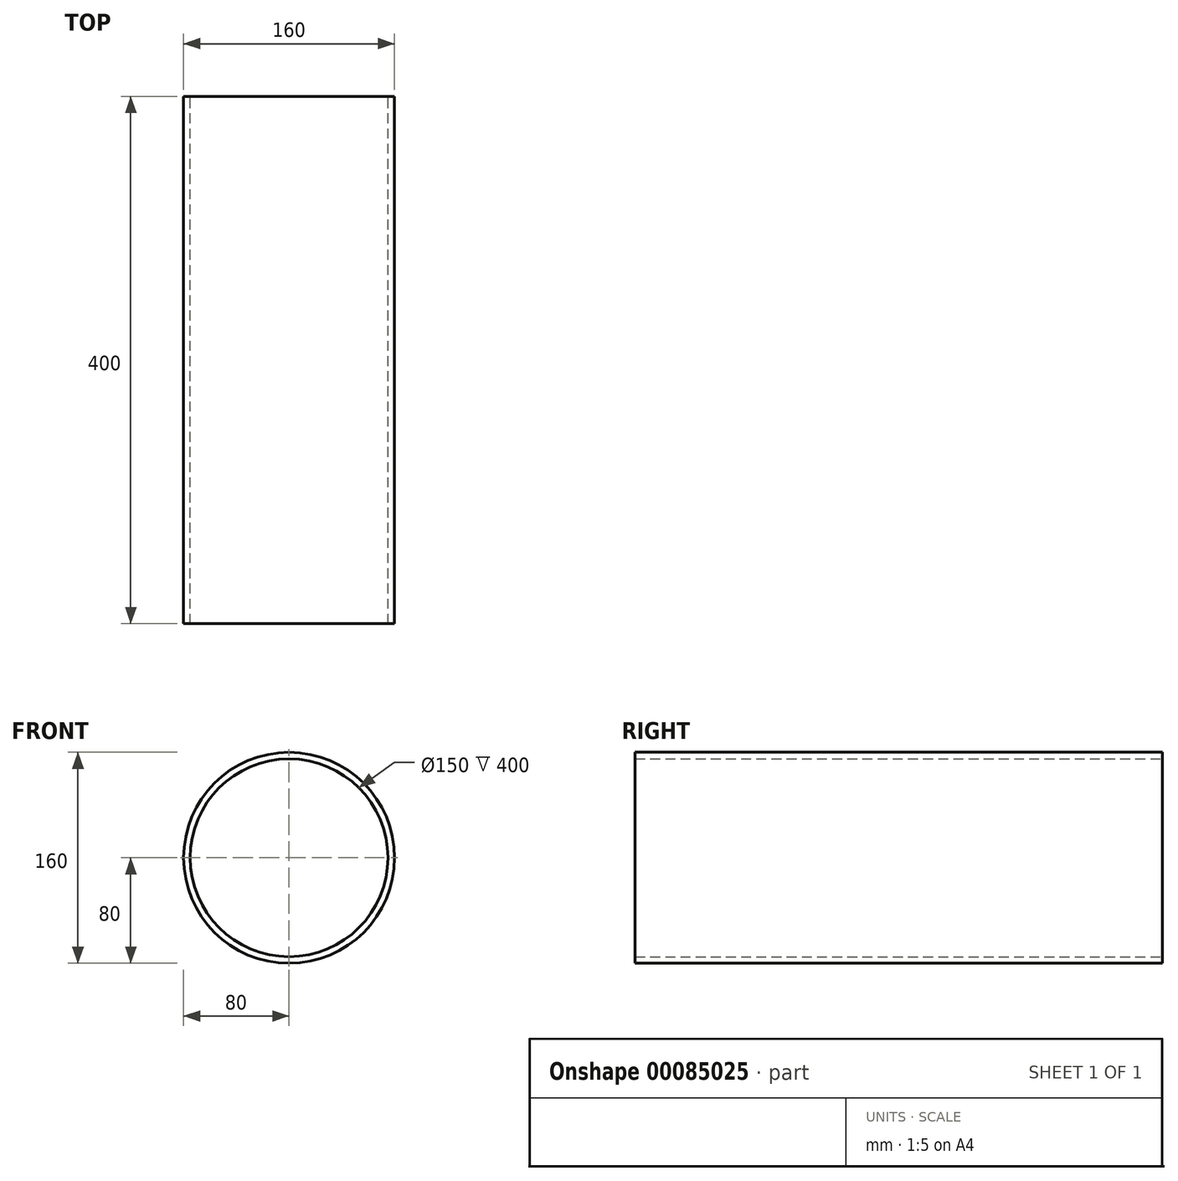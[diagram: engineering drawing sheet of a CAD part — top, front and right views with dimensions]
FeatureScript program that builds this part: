
annotation { "Feature Type Name" : "Feature", "Feature Type Description" : "" }
export const myFeature = defineFeature(function(context is Context, id is Id, definition is map)
    precondition{}
    {
        {
            var Q0;
            Q0=qCreatedBy(makeId("Front.planeOp"),FACE);
            var sketch = newSketch(context, id + "F0", { "sketchPlane" : qUnion([Q0])});
            skCircle(sketch, "E0", {"center": v(0, 0) * mm, "radius": 80 * mm});
            skLineSegment(sketch, "E1", {"start": v(0, 0) * mm, "end": v(0, 80) * mm});
            skCircle(sketch, "E2", {"center": v(0, 0) * mm, "radius": 75 * mm});
            skLineSegment(sketch, "E3", {"start": v(0, 0) * mm, "end": v(46.6, 58.77) * mm});
            skSolve(sketch);
        }
        {
            var Q0;
            Q0 = qSketchRegion(id + "F0", true);
            extrude(context, id + "F1", {"entities" : qUnion([Q0]), "depth" : 400 * mm});
        }
    });
